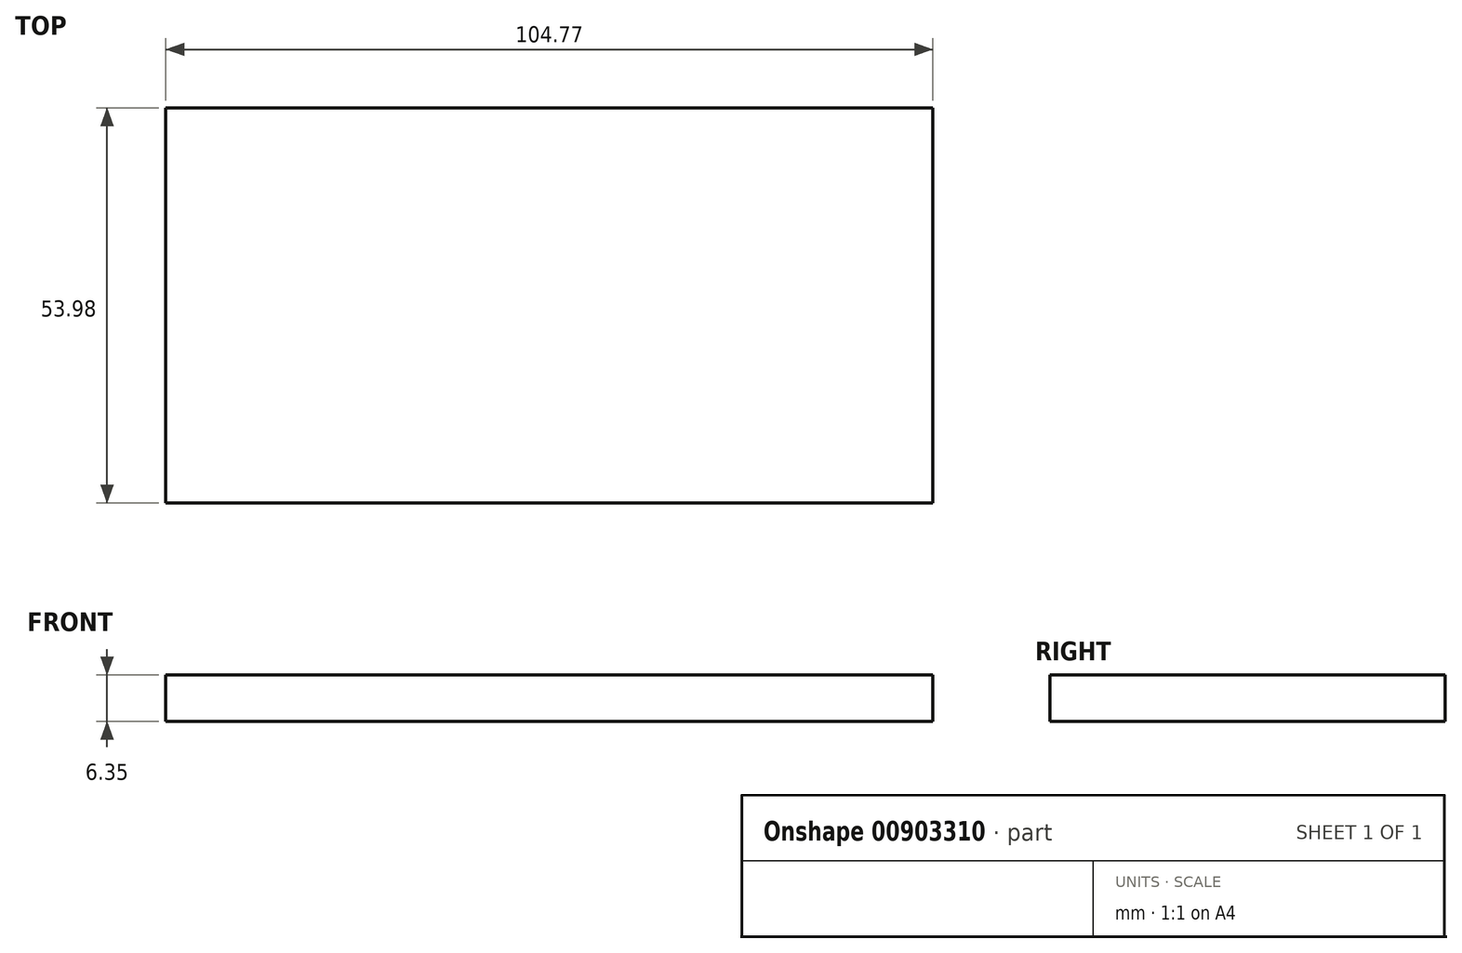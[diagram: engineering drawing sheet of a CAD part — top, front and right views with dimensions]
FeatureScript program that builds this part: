
annotation { "Feature Type Name" : "Feature", "Feature Type Description" : "" }
export const myFeature = defineFeature(function(context is Context, id is Id, definition is map)
    precondition{}
    {
        {
            var Q0;
            Q0=qCreatedBy(makeId("Top.planeOp"),FACE);
            var sketch = newSketch(context, id + "F0", { "sketchPlane" : qUnion([Q0])});
            skLineSegment(sketch, "E0.bottom", {"start": v(0, 0) * mm, "end": v(104.78, 0) * mm});
            skLineSegment(sketch, "E0.top", {"start": v(0, -53.97) * mm, "end": v(104.78, -53.97) * mm});
            skLineSegment(sketch, "E0.left", {"start": v(0, 0) * mm, "end": v(0, -53.97) * mm});
            skLineSegment(sketch, "E0.right", {"start": v(104.78, 0) * mm, "end": v(104.78, -53.97) * mm});
            skSolve(sketch);
        }
        {
            var Q0;
            Q0=makeQuery(id+"F0.imprint","IMPRINT",FACE,{"disambiguationData":[TD([[makeQuery(id+"F0.imprint","IMPRINT",EDGE,{"derivedFrom":sQuery(id+"F0.wireOp",EDGE,"E0.bottom")}),-1.0]])]});
            extrude(context, id + "F1", {"entities" : qUnion([Q0]), "depth" : 6.35 * mm, "offsetDistance" : 25.4 * mm});
        }
    });
